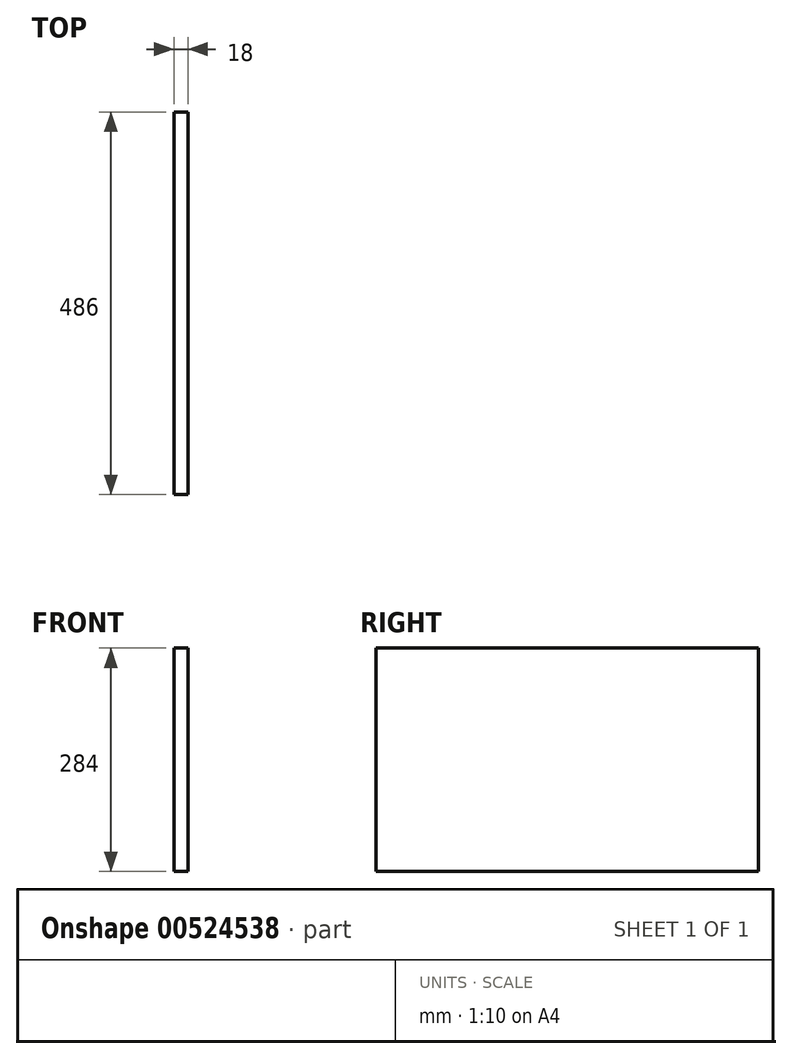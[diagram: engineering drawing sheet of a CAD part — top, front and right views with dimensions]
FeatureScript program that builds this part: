
annotation { "Feature Type Name" : "Feature", "Feature Type Description" : "" }
export const myFeature = defineFeature(function(context is Context, id is Id, definition is map)
    precondition{}
    {
        {
            var Q0;
            Q0=qCreatedBy(makeId("Right.planeOp"),FACE);
            var sketch = newSketch(context, id + "F0", { "sketchPlane" : qUnion([Q0])});
            skLineSegment(sketch, "E0.bottom", {"start": v(0, 0) * mm, "end": v(486, 0) * mm});
            skLineSegment(sketch, "E0.top", {"start": v(0, 284) * mm, "end": v(486, 284) * mm});
            skLineSegment(sketch, "E0.left", {"start": v(0, 0) * mm, "end": v(0, 284) * mm});
            skLineSegment(sketch, "E0.right", {"start": v(486, 0) * mm, "end": v(486, 284) * mm});
            skSolve(sketch);
        }
        {
            var Q0;
            Q0 = qSketchRegion(id + "F0", true);
            extrude(context, id + "F1", {"entities" : qUnion([Q0]), "depth" : 18 * mm, "offsetDistance" : 25 * mm});
        }
    });
